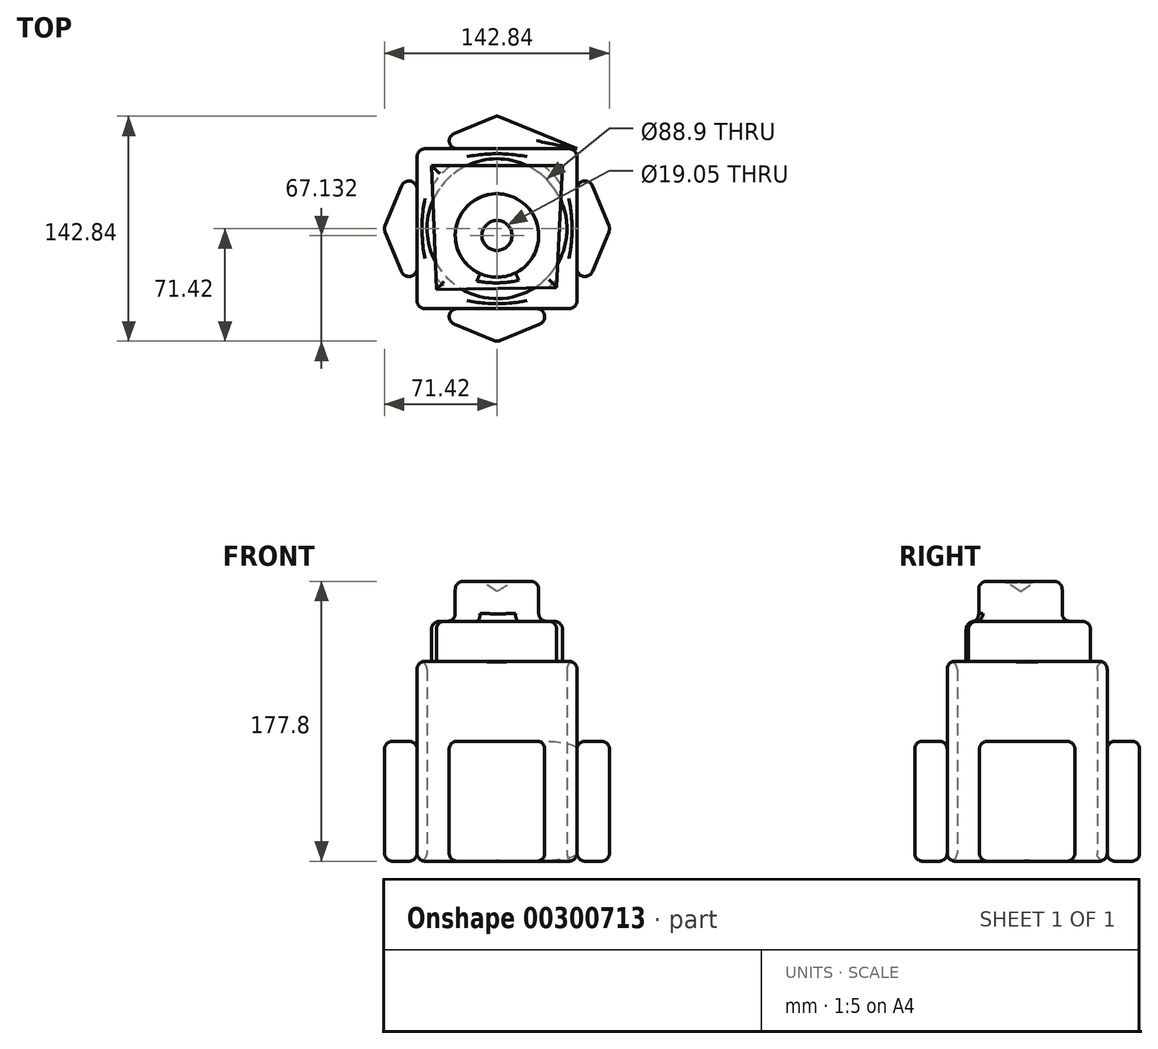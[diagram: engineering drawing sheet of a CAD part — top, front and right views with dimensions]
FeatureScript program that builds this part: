
annotation { "Feature Type Name" : "Feature", "Feature Type Description" : "" }
export const myFeature = defineFeature(function(context is Context, id is Id, definition is map)
    precondition{}
    {
        {
            var Q0;
            Q0=qCreatedBy(makeId("Top.planeOp"),FACE);
            var sketch = newSketch(context, id + "F0", { "sketchPlane" : qUnion([Q0])});
            skLineSegment(sketch, "E0.bottom", {"start": v(-50.8, 50.8) * mm, "end": v(50.8, 50.8) * mm});
            skLineSegment(sketch, "E0.top", {"start": v(-50.8, -50.8) * mm, "end": v(50.8, -50.8) * mm});
            skLineSegment(sketch, "E0.left", {"start": v(-50.8, 50.8) * mm, "end": v(-50.8, -50.8) * mm});
            skLineSegment(sketch, "E0.right", {"start": v(50.8, 50.8) * mm, "end": v(50.8, -50.8) * mm});
            skPoint(sketch, "E0.middle", {"position": v(0, 0) * mm});
            skCircle(sketch, "E1.cCircle", {"center": v(0, 0) * mm, "radius": 71.84 * mm, "construction": true});
            skLineSegment(sketch, "E1.0", {"start": v(50.8, 50.8) * mm, "end": v(71.84, 0) * mm});
            skLineSegment(sketch, "E1.1", {"start": v(71.84, 0) * mm, "end": v(50.8, -50.8) * mm});
            skLineSegment(sketch, "E1.2", {"start": v(50.8, -50.8) * mm, "end": v(0, -71.84) * mm});
            skLineSegment(sketch, "E1.3", {"start": v(0, -71.84) * mm, "end": v(-50.8, -50.8) * mm});
            skLineSegment(sketch, "E1.4", {"start": v(-50.8, -50.8) * mm, "end": v(-71.84, 0) * mm});
            skLineSegment(sketch, "E1.5", {"start": v(-71.84, 0) * mm, "end": v(-50.8, 50.8) * mm});
            skLineSegment(sketch, "E1.6", {"start": v(-50.8, 50.8) * mm, "end": v(0, 71.84) * mm});
            skLineSegment(sketch, "E1.7", {"start": v(0, 71.84) * mm, "end": v(50.8, 50.8) * mm});
            skSolve(sketch);
        }
        {
            var Q0;
            Q0=makeQuery(id+"F0.imprint","IMPRINT",FACE,{"disambiguationData":[TD([[makeQuery(id+"F0.imprint","IMPRINT",EDGE,{"derivedFrom":sQuery(id+"F0.wireOp",EDGE,"E0.bottom")}),1.0]])]});
            var Q1;
            Q1=makeQuery(id+"F0.imprint","IMPRINT",FACE,{"disambiguationData":[TD([[makeQuery(id+"F0.imprint","IMPRINT",EDGE,{"derivedFrom":sQuery(id+"F0.wireOp",EDGE,"E0.top")}),-1.0]])]});
            var Q2;
            Q2=makeQuery(id+"F0.imprint","IMPRINT",FACE,{"disambiguationData":[TD([[makeQuery(id+"F0.imprint","IMPRINT",EDGE,{"derivedFrom":sQuery(id+"F0.wireOp",EDGE,"E0.left")}),-1.0]])]});
            var Q3;
            Q3=makeQuery(id+"F0.imprint","IMPRINT",FACE,{"disambiguationData":[TD([[makeQuery(id+"F0.imprint","IMPRINT",EDGE,{"derivedFrom":sQuery(id+"F0.wireOp",EDGE,"E0.right")}),1.0]])]});
            extrude(context, id + "F1", {"entities" : qUnion([Q0, Q1, Q2, Q3]), "depth" : 76.2 * mm});
        }
        {
            var Q0;
            Q0=makeQuery(id+"F0.imprint","IMPRINT",FACE,{"disambiguationData":[TD([[makeQuery(id+"F0.imprint","IMPRINT",EDGE,{"derivedFrom":sQuery(id+"F0.wireOp",EDGE,"E0.bottom")}),-1.0]])]});
            extrude(context, id + "F2", {"entities" : qUnion([Q0]), "depth" : 127 * mm});
        }
        {
            var Q0;
            Q0=makeQuery(id+"F2.opExtrude","CAP_FACE",FACE,{"disambiguationData":[OSD([sQuery(id+"F0.wireOp",EDGE,"E0.bottom"),sQuery(id+"F0.wireOp",EDGE,"E0.top"),sQuery(id+"F0.wireOp",EDGE,"E0.left"),sQuery(id+"F0.wireOp",EDGE,"E0.right")])],"isStart":false});
            var sketch = newSketch(context, id + "F3", { "sketchPlane" : qUnion([Q0])});
            skSolve(sketch);
        }
        {
            var Q0;
            Q0=sQuery(id+"F0.wireOp",VERTEX,"E0.middle");
            var Q1;
            Q1=makeQuery(id+"F2.opExtrude","SWEPT_BODY",BODY,{"disambiguationData":[OSD([sQuery(id+"F0.wireOp",EDGE,"E0.bottom"),sQuery(id+"F0.wireOp",EDGE,"E0.top"),sQuery(id+"F0.wireOp",EDGE,"E0.left"),sQuery(id+"F0.wireOp",EDGE,"E0.right")])]});
            hole(context, id + "F4", {"style" : HoleStyle.SIMPLE, "endStyle" : HoleEndStyle.THROUGH, "oppositeDirection" : true, "holeDiameter" : 88.9 * mm, "tappedDepth" : 12.7 * mm, "tapClearance" : 3, "locations" : qUnion([Q0]), "scope" : qUnion([Q1])});
        }
        {
            var Q0;
            Q0=makeQuery(id+"F1.opExtrude","CAP_FACE",FACE,{"disambiguationData":[OSD([sQuery(id+"F0.wireOp",EDGE,"E0.right"),sQuery(id+"F0.wireOp",EDGE,"E1.0"),sQuery(id+"F0.wireOp",EDGE,"E1.1")])],"isStart":false});
            fillet(context, id + "F5", {"entities" : qUnion([Q0]), "radius" : 5.08 * mm, "tangentPropagation" : true, "allowEdgeOverflow" : false});
        }
        {
            var Q0;
            Q0=makeQuery(id+"F1.opExtrude","CAP_FACE",FACE,{"disambiguationData":[OSD([sQuery(id+"F0.wireOp",EDGE,"E0.top"),sQuery(id+"F0.wireOp",EDGE,"E1.2"),sQuery(id+"F0.wireOp",EDGE,"E1.3")])],"isStart":false});
            var Q1;
            Q1=makeQuery(id+"F1.opExtrude","CAP_FACE",FACE,{"disambiguationData":[OSD([sQuery(id+"F0.wireOp",EDGE,"E0.left"),sQuery(id+"F0.wireOp",EDGE,"E1.4"),sQuery(id+"F0.wireOp",EDGE,"E1.5")])],"isStart":false});
            var Q2;
            Q2=makeQuery(id+"F1.opExtrude","CAP_FACE",FACE,{"disambiguationData":[OSD([sQuery(id+"F0.wireOp",EDGE,"E0.bottom"),sQuery(id+"F0.wireOp",EDGE,"E1.6"),sQuery(id+"F0.wireOp",EDGE,"E1.7")])],"isStart":false});
            fillet(context, id + "F6", {"entities" : qUnion([Q0, Q1, Q2]), "radius" : 5.08 * mm, "tangentPropagation" : true, "allowEdgeOverflow" : false});
        }
        {
            var Q0;
            Q0=makeQuery(id+"F1.opExtrude","CAP_EDGE",EDGE,{"disambiguationData":[OSD([sQuery(id+"F0.wireOp",EDGE,"E0.bottom")])],"isStart":true});
            var Q1;
            Q1=makeQuery(id+"F1.opExtrude","CAP_FACE",FACE,{"disambiguationData":[OSD([sQuery(id+"F0.wireOp",EDGE,"E0.left"),sQuery(id+"F0.wireOp",EDGE,"E1.4"),sQuery(id+"F0.wireOp",EDGE,"E1.5")])],"isStart":true});
            var Q2;
            Q2=makeQuery(id+"F1.opExtrude","CAP_FACE",FACE,{"disambiguationData":[OSD([sQuery(id+"F0.wireOp",EDGE,"E0.top"),sQuery(id+"F0.wireOp",EDGE,"E1.2"),sQuery(id+"F0.wireOp",EDGE,"E1.3")])],"isStart":true});
            var Q3;
            Q3=makeQuery(id+"F1.opExtrude","CAP_FACE",FACE,{"disambiguationData":[OSD([sQuery(id+"F0.wireOp",EDGE,"E0.right"),sQuery(id+"F0.wireOp",EDGE,"E1.0"),sQuery(id+"F0.wireOp",EDGE,"E1.1")])],"isStart":true});
            var Q4;
            Q4=makeQuery(id+"F1.opExtrude","CAP_FACE",FACE,{"disambiguationData":[OSD([sQuery(id+"F0.wireOp",EDGE,"E0.bottom"),sQuery(id+"F0.wireOp",EDGE,"E1.6"),sQuery(id+"F0.wireOp",EDGE,"E1.7")])],"isStart":true});
            fillet(context, id + "F7", {"entities" : qUnion([Q0, Q1, Q2, Q3, Q4]), "radius" : 5.08 * mm, "tangentPropagation" : true, "allowEdgeOverflow" : false});
        }
        {
            var Q0;
            Q0=makeQuery(id+"F2.opExtrude","CAP_FACE",FACE,{"disambiguationData":[OSD([sQuery(id+"F0.wireOp",EDGE,"E0.bottom"),sQuery(id+"F0.wireOp",EDGE,"E0.top"),sQuery(id+"F0.wireOp",EDGE,"E0.left"),sQuery(id+"F0.wireOp",EDGE,"E0.right")])],"isStart":false});
            fillet(context, id + "F8", {"entities" : qUnion([Q0]), "radius" : 5.08 * mm, "tangentPropagation" : true, "allowEdgeOverflow" : false});
        }
        {
            var Q0;
            Q0=makeQuery(id+"F1.opExtrude","SWEPT_FACE",FACE,{"disambiguationData":[OSD([sQuery(id+"F0.wireOp",EDGE,"E1.5")])]});
            var Q1;
            Q1=makeQuery(id+"F1.opExtrude","SWEPT_FACE",FACE,{"disambiguationData":[OSD([sQuery(id+"F0.wireOp",EDGE,"E1.6")])]});
            var Q2;
            Q2=makeQuery(id+"F1.opExtrude","SWEPT_FACE",FACE,{"disambiguationData":[OSD([sQuery(id+"F0.wireOp",EDGE,"E1.4")])]});
            var Q3;
            Q3=makeQuery(id+"F1.opExtrude","SWEPT_FACE",FACE,{"disambiguationData":[OSD([sQuery(id+"F0.wireOp",EDGE,"E1.3")])]});
            var Q4;
            Q4=makeQuery(id+"F1.opExtrude","SWEPT_FACE",FACE,{"disambiguationData":[OSD([sQuery(id+"F0.wireOp",EDGE,"E1.0")])]});
            var Q5;
            Q5=makeQuery(id+"F1.opExtrude","SWEPT_FACE",FACE,{"disambiguationData":[OSD([sQuery(id+"F0.wireOp",EDGE,"E1.1")])]});
            fillet(context, id + "F9", {"entities" : qUnion([Q0, Q1, Q2, Q3, Q4, Q5]), "radius" : 5.08 * mm, "tangentPropagation" : true, "allowEdgeOverflow" : false});
        }
        {
            var Q0;
            Q0=makeQuery(id+"F1.opExtrude","SWEPT_FACE",FACE,{"disambiguationData":[OSD([sQuery(id+"F0.wireOp",EDGE,"E1.2")])]});
            var Q1;
            Q1=makeQuery(id+"F2.opExtrude","SWEPT_FACE",FACE,{"disambiguationData":[OSD([sQuery(id+"F0.wireOp",EDGE,"E0.top")])]});
            var Q2;
            Q2=makeQuery(id+"F2.opExtrude","SWEPT_EDGE",EDGE,{"disambiguationData":[OSD([sQuery(id+"F0.wireOp",EDGE,"E0.bottom"),sQuery(id+"F0.wireOp",EDGE,"E0.left"),sQuery(id+"F0.wireOp",EDGE,"E1.5"),sQuery(id+"F0.wireOp",EDGE,"E1.6")])]});
            var Q3;
            Q3=makeQuery(id+"F2.opExtrude","SWEPT_FACE",FACE,{"disambiguationData":[OSD([sQuery(id+"F0.wireOp",EDGE,"E0.left")])]});
            var Q4;
            Q4=makeQuery(id+"F2.opExtrude","SWEPT_FACE",FACE,{"disambiguationData":[OSD([sQuery(id+"F0.wireOp",EDGE,"E0.bottom")])]});
            var Q5;
            Q5=makeQuery(id+"F2.opExtrude","SWEPT_FACE",FACE,{"disambiguationData":[OSD([sQuery(id+"F0.wireOp",EDGE,"E0.right")])]});
            var Q6;
            Q6=makeQuery(id+"F2.opExtrude","CAP_FACE",FACE,{"disambiguationData":[OSD([sQuery(id+"F0.wireOp",EDGE,"E0.bottom"),sQuery(id+"F0.wireOp",EDGE,"E0.top"),sQuery(id+"F0.wireOp",EDGE,"E0.left"),sQuery(id+"F0.wireOp",EDGE,"E0.right")])],"isStart":true});
            fillet(context, id + "F10", {"entities" : qUnion([Q0, Q1, Q2, Q3, Q4, Q5, Q6]), "radius" : 5.08 * mm, "tangentPropagation" : true, "allowEdgeOverflow" : false});
        }
        {
            var Q0;
            Q0=makeQuery(id+"F3.imprint","IMPRINT",FACE,{"disambiguationData":[TD([[makeQuery(id+"F3.imprint","IMPRINT",EDGE,{"derivedFrom":makeQuery(id+"F2.opExtrude","CAP_EDGE",EDGE,{"disambiguationData":[OSD([sQuery(id+"F0.wireOp",EDGE,"E0.bottom")])],"isStart":false})}),-1.0]])]});
            var sketch = newSketch(context, id + "F11", { "sketchPlane" : qUnion([Q0])});
            skLineSegment(sketch, "E2", {"start": v(37.89, -37.23) * mm, "end": v(-41.55, 40.13) * mm});
            skLineSegment(sketch, "E3", {"start": v(-41.55, 40.13) * mm, "end": v(-38.47, -38.75) * mm});
            skLineSegment(sketch, "E4", {"start": v(-38.47, -38.75) * mm, "end": v(41.6, 40.13) * mm});
            skLineSegment(sketch, "E5", {"start": v(41.6, 40.13) * mm, "end": v(37.89, -37.23) * mm});
            skLineSegment(sketch, "E6", {"start": v(37.89, -37.23) * mm, "end": v(-38.47, -38.75) * mm});
            skLineSegment(sketch, "E7", {"start": v(-41.55, 40.13) * mm, "end": v(41.6, 40.13) * mm});
            skSolve(sketch);
        }
        {
            var Q0;
            {var subQ0=sQuery(id+"F11.wireOp",EDGE,"E6");Q0=makeQuery(id+"F11.imprint","IMPRINT",FACE,{"disambiguationData":[TD([[makeQuery(id+"F11.imprint","IMPRINT",EDGE,{"derivedFrom":subQ0}),-1.0]])]});}
            var Q1;
            {var subQ0=sQuery(id+"F11.wireOp",EDGE,"E3");Q1=makeQuery(id+"F11.imprint","IMPRINT",FACE,{"disambiguationData":[TD([[makeQuery(id+"F11.imprint","IMPRINT",EDGE,{"derivedFrom":subQ0}),1.0]])]});}
            var Q2;
            {var subQ0=sQuery(id+"F11.wireOp",EDGE,"E5");Q2=makeQuery(id+"F11.imprint","IMPRINT",FACE,{"disambiguationData":[TD([[makeQuery(id+"F11.imprint","IMPRINT",EDGE,{"derivedFrom":subQ0}),-1.0]])]});}
            var Q3;
            {var subQ0=sQuery(id+"F11.wireOp",EDGE,"E7");Q3=makeQuery(id+"F11.imprint","IMPRINT",FACE,{"disambiguationData":[TD([[makeQuery(id+"F11.imprint","IMPRINT",EDGE,{"derivedFrom":subQ0}),-1.0]])]});}
            extrude(context, id + "F12", {"entities" : qUnion([Q0, Q1, Q2, Q3]), "operationType" : NewBodyOperationType.ADD, "depth" : 25.4 * mm});
        }
        {
            var Q0;
            Q0=makeQuery(id+"F12.opExtrude","CAP_FACE",FACE,{"disambiguationData":[OSD([sQuery(id+"F11.wireOp",EDGE,"E3"),sQuery(id+"F11.wireOp",EDGE,"E5"),sQuery(id+"F11.wireOp",EDGE,"E6"),sQuery(id+"F11.wireOp",EDGE,"E7")])],"isStart":false});
            fillet(context, id + "F13", {"entities" : qUnion([Q0]), "radius" : 5.08 * mm, "tangentPropagation" : true, "allowEdgeOverflow" : false});
        }
        {
            var Q0;
            Q0=makeQuery(id+"F12.opExtrude","CAP_FACE",FACE,{"disambiguationData":[OSD([sQuery(id+"F11.wireOp",EDGE,"E3"),sQuery(id+"F11.wireOp",EDGE,"E5"),sQuery(id+"F11.wireOp",EDGE,"E6"),sQuery(id+"F11.wireOp",EDGE,"E7")])],"isStart":false});
            var sketch = newSketch(context, id + "F14", { "sketchPlane" : qUnion([Q0])});
            skArc(sketch, "E8", {"start": v(-34.9, 0) * mm, "mid": v(-0.16, -4.29) * mm, "end": v(34.59, 0) * mm});
            skCircle(sketch, "E9", {"center": v(0, -4.29) * mm, "radius": 26.5 * mm});
            skSolve(sketch);
        }
        {
            var Q0;
            {var subQ0=sQuery(id+"F14.wireOp",EDGE,"E9");var subQ1=sQuery(id+"F14.wireOp",EDGE,"E8");var subQ2=makeQuery(id+"F14.imprint","INTERSECT",VERTEX,{"disambiguationData":[OD(0.0)],"derivedFrom":[subQ1,subQ0]});Q0=makeQuery(id+"F14.imprint","IMPRINT",FACE,{"disambiguationData":[TD([[makeQuery(id+"F14.imprint","IMPRINT",EDGE,{"disambiguationData":[TD([[subQ2,-1.0]])],"derivedFrom":subQ1}),1.0]])]});}
            var Q1;
            {var subQ0=sQuery(id+"F14.wireOp",EDGE,"E9");var subQ1=sQuery(id+"F14.wireOp",EDGE,"E8");var subQ2=makeQuery(id+"F14.imprint","INTERSECT",VERTEX,{"disambiguationData":[OD(0.0)],"derivedFrom":[subQ1,subQ0]});Q1=makeQuery(id+"F14.imprint","IMPRINT",FACE,{"disambiguationData":[TD([[makeQuery(id+"F14.imprint","IMPRINT",EDGE,{"disambiguationData":[TD([[subQ2,-1.0]])],"derivedFrom":subQ1}),-1.0]])]});}
            extrude(context, id + "F15", {"entities" : qUnion([Q0, Q1]), "operationType" : NewBodyOperationType.ADD, "depth" : 25.4 * mm});
        }
        {
            var Q0;
            Q0=makeQuery(id+"F15.opExtrude","CAP_FACE",FACE,{"disambiguationData":[OSD([sQuery(id+"F14.wireOp",EDGE,"E9")])],"isStart":false});
            var Q1;
            Q1=makeQuery(id+"F15.opExtrude","SWEPT_FACE",FACE,{"disambiguationData":[OSD([sQuery(id+"F14.wireOp",EDGE,"E9")])]});
            fillet(context, id + "F16", {"entities" : qUnion([Q0, Q1]), "radius" : 5.08 * mm, "tangentPropagation" : true, "allowEdgeOverflow" : false});
        }
        {
            var Q0;
            Q0=makeQuery(id+"F15.opExtrude","CAP_FACE",FACE,{"disambiguationData":[OSD([sQuery(id+"F14.wireOp",EDGE,"E9")])],"isStart":false});
            var sketch = newSketch(context, id + "F17", { "sketchPlane" : qUnion([Q0])});
            skPoint(sketch, "E10", {"position": v(0, -4.29) * mm});
            skSolve(sketch);
        }
        {
            var Q0;
            Q0=sQuery(id+"F17.wireOp",VERTEX,"E10");
            var Q1;
            Q1=makeQuery(id+"F2.opExtrude","SWEPT_BODY",BODY,{"disambiguationData":[OSD([sQuery(id+"F0.wireOp",EDGE,"E0.bottom"),sQuery(id+"F0.wireOp",EDGE,"E0.top"),sQuery(id+"F0.wireOp",EDGE,"E0.left"),sQuery(id+"F0.wireOp",EDGE,"E0.right")])]});
            hole(context, id + "F18", {"style" : HoleStyle.SIMPLE, "endStyle" : HoleEndStyle.BLIND, "holeDiameter" : 19.05 * mm, "holeDepth" : 0.64 * mm, "tappedDepth" : 12.7 * mm, "tapClearance" : 3, "locations" : qUnion([Q0]), "scope" : qUnion([Q1])});
        }
    });
